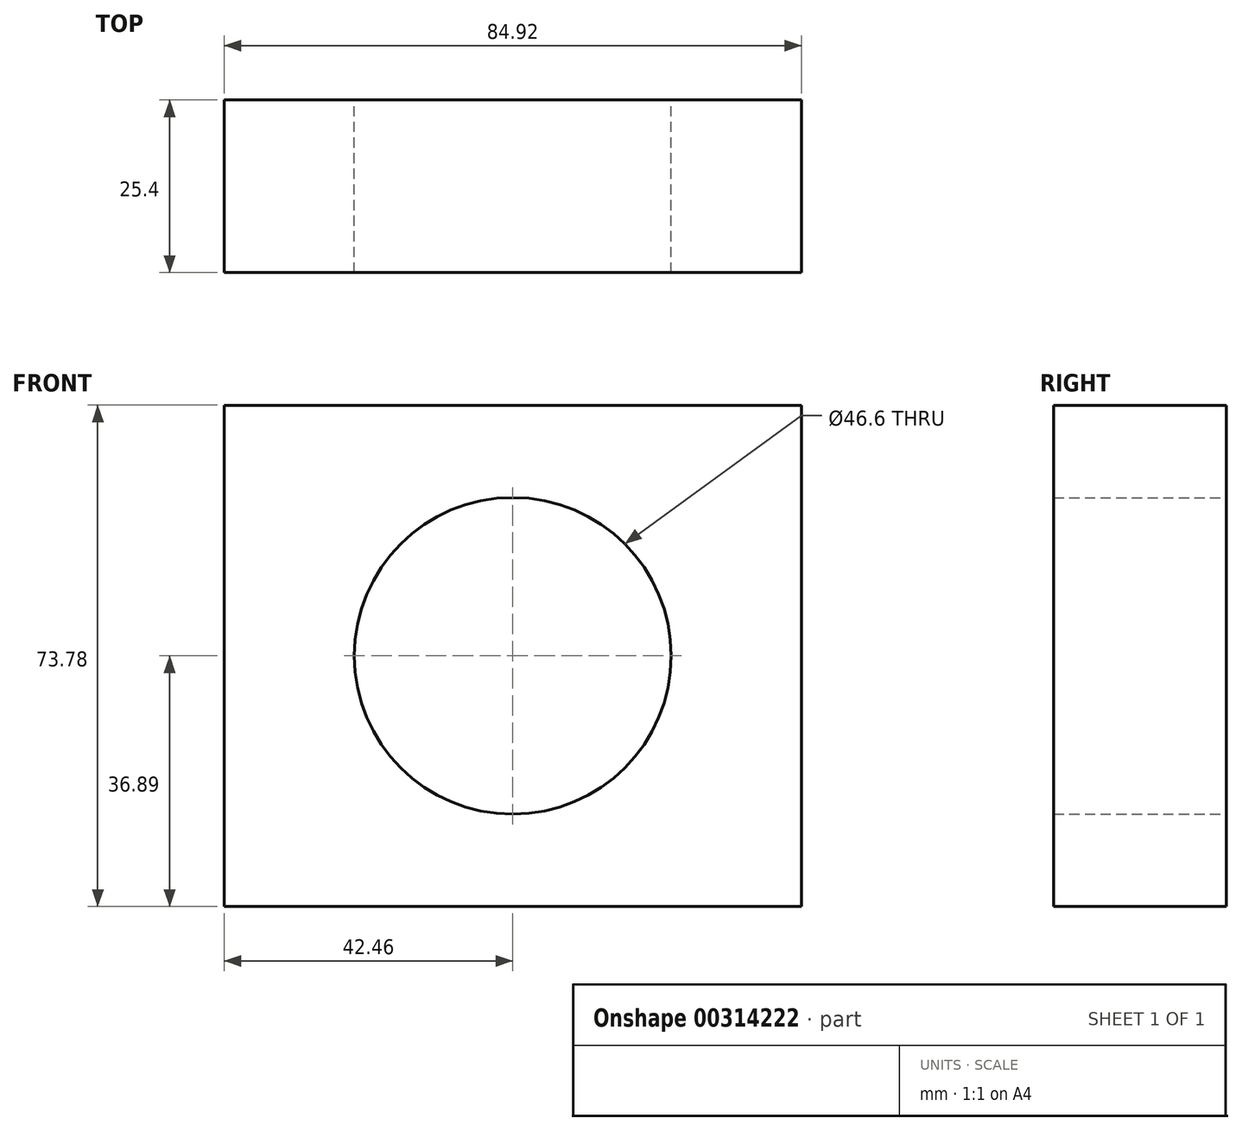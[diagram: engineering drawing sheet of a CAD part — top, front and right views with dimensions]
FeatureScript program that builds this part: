
annotation { "Feature Type Name" : "Feature", "Feature Type Description" : "" }
export const myFeature = defineFeature(function(context is Context, id is Id, definition is map)
    precondition{}
    {
        {
            var Q0;
            Q0=qCreatedBy(makeId("Front.planeOp"),FACE);
            var sketch = newSketch(context, id + "F0", { "sketchPlane" : qUnion([Q0])});
            skLineSegment(sketch, "E0.bottom", {"start": v(42.46, 36.89) * mm, "end": v(-42.46, 36.89) * mm});
            skLineSegment(sketch, "E0.top", {"start": v(42.46, -36.89) * mm, "end": v(-42.46, -36.89) * mm});
            skLineSegment(sketch, "E0.left", {"start": v(42.46, 36.89) * mm, "end": v(42.46, -36.89) * mm});
            skLineSegment(sketch, "E0.right", {"start": v(-42.46, 36.89) * mm, "end": v(-42.46, -36.89) * mm});
            skPoint(sketch, "E0.middle", {"position": v(0, 0) * mm});
            skCircle(sketch, "E1", {"center": v(0, 0) * mm, "radius": 23.3 * mm});
            skSolve(sketch);
        }
        {
            var Q0;
            Q0=makeQuery(id+"F0.imprint","IMPRINT",FACE,{"disambiguationData":[TD([[makeQuery(id+"F0.imprint","IMPRINT",EDGE,{"derivedFrom":sQuery(id+"F0.wireOp",EDGE,"E0.bottom")}),1.0]])]});
            extrude(context, id + "F1", {"entities" : qUnion([Q0]), "depth" : 25.4 * mm});
        }
    });
